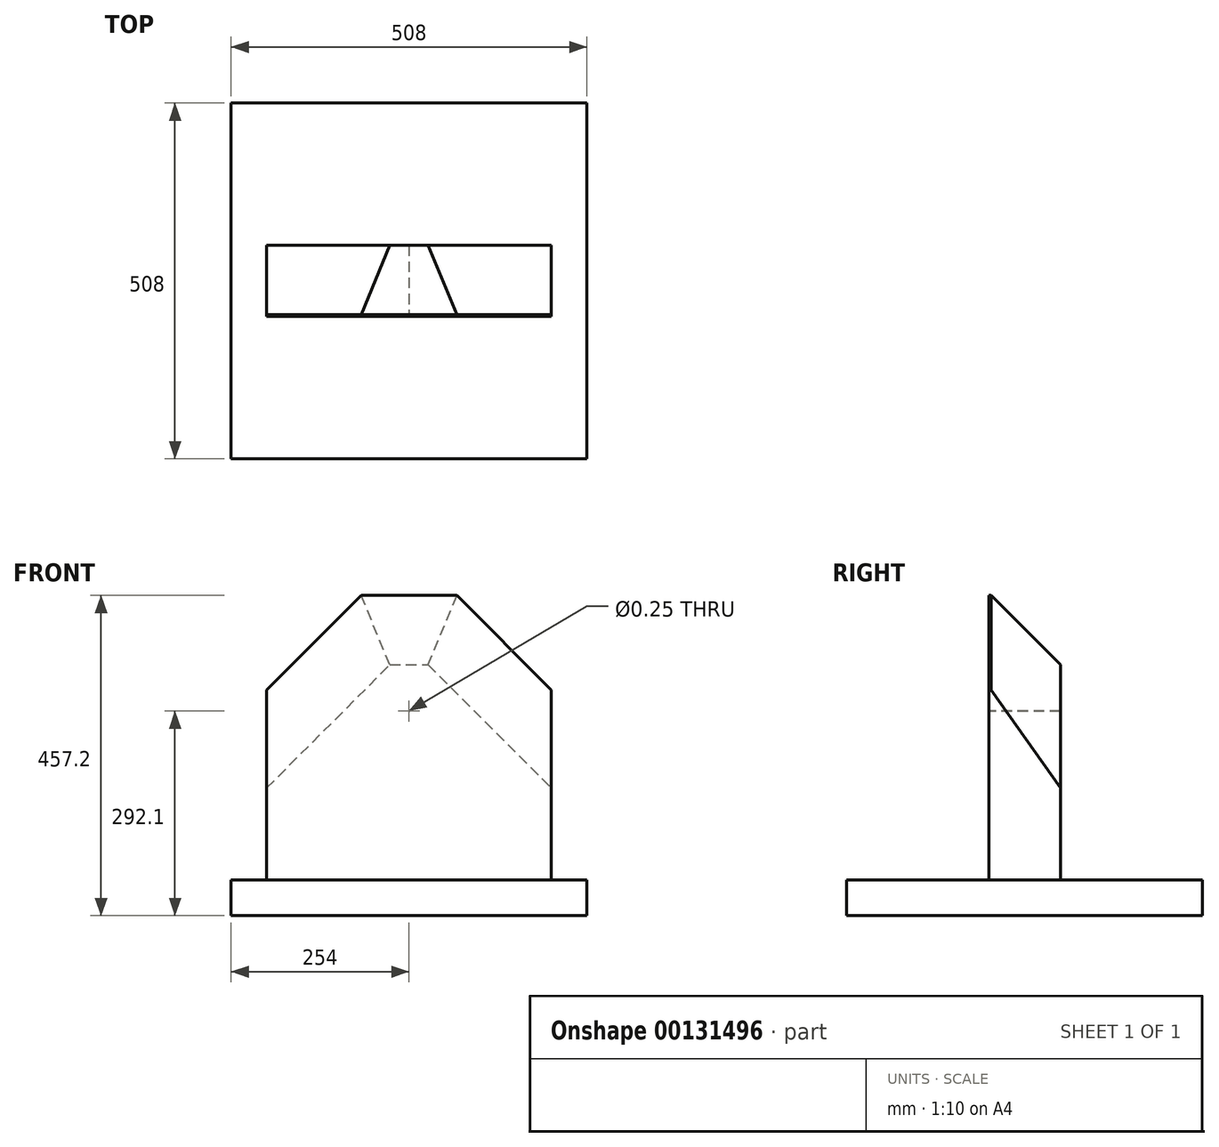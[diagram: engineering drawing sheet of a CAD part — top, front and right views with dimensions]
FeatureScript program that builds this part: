
annotation { "Feature Type Name" : "Feature", "Feature Type Description" : "" }
export const myFeature = defineFeature(function(context is Context, id is Id, definition is map)
    precondition{}
    {
        {
            assignVariable(context, id + "F0", {"name" : "A_Axis", "anyValue" : 60 - 60});
        }
        {
            assignVariable(context, id + "F1", {"name" : "C_Axis", "anyValue" : 35.3 - 35.3});
        }
        {
            var Q0;
            Q0=qCreatedBy(makeId("Top.planeOp"),FACE);
            var sketch = newSketch(context, id + "F2", { "sketchPlane" : qUnion([Q0])});
            skLineSegment(sketch, "E0", {"start": v(0, 0) * mm, "end": v(0, 502.81) * mm, "construction": true});
            skLineSegment(sketch, "E1", {"start": v(0, 0) * mm, "end": v(606.98, 0) * mm, "construction": true});
            skSolve(sketch);
        }
        {
            var Q0;
            Q0=qCreatedBy(makeId("Top.planeOp"),FACE);
            var sketch = newSketch(context, id + "F3", { "sketchPlane" : qUnion([Q0])});
            skLineSegment(sketch, "E2.bottom", {"start": v(254, 254) * mm, "end": v(-254, 254) * mm});
            skLineSegment(sketch, "E2.top", {"start": v(254, -254) * mm, "end": v(-254, -254) * mm});
            skLineSegment(sketch, "E2.left", {"start": v(254, 254) * mm, "end": v(254, -254) * mm});
            skLineSegment(sketch, "E2.right", {"start": v(-254, 254) * mm, "end": v(-254, -254) * mm});
            skPoint(sketch, "E2.middle", {"position": v(0, 0) * mm});
            skSolve(sketch);
        }
        {
            var Q0;
            Q0 = qSketchRegion(id + "F3", true);
            extrude(context, id + "F4", {"entities" : qUnion([Q0]), "depth" : 50.8 * mm});
        }
        {
            var Q0;
            Q0=makeQuery(id+"F4.opExtrude","CAP_FACE",FACE,{"disambiguationData":[OSD([sQuery(id+"F3.wireOp",EDGE,"E2.bottom"),sQuery(id+"F3.wireOp",EDGE,"E2.top"),sQuery(id+"F3.wireOp",EDGE,"E2.left"),sQuery(id+"F3.wireOp",EDGE,"E2.right")])],"isStart":false});
            var sketch = newSketch(context, id + "F5", { "sketchPlane" : qUnion([Q0])});
            skLineSegment(sketch, "E3.bottom", {"start": v(-203.2, 50.8) * mm, "end": v(203.2, 50.8) * mm});
            skLineSegment(sketch, "E3.top", {"start": v(-203.2, -50.8) * mm, "end": v(203.2, -50.8) * mm});
            skLineSegment(sketch, "E3.left", {"start": v(-203.2, 50.8) * mm, "end": v(-203.2, -50.8) * mm});
            skLineSegment(sketch, "E3.right", {"start": v(203.2, 50.8) * mm, "end": v(203.2, -50.8) * mm});
            skPoint(sketch, "E3.middle", {"position": v(0, 0) * mm});
            skSolve(sketch);
        }
        {
            var Q0;
            Q0 = qSketchRegion(id + "F5", true);
            extrude(context, id + "F6", {"entities" : qUnion([Q0]), "operationType" : NewBodyOperationType.ADD, "depth" : 406.4 * mm});
        }
        {
            var Q0;
            Q0=makeQuery(id+"F6.opExtrude","SWEPT_FACE",FACE,{"disambiguationData":[OSD([sQuery(id+"F5.wireOp",EDGE,"E3.top")])]});
            var sketch = newSketch(context, id + "F7", { "sketchPlane" : qUnion([Q0])});
            skLineSegment(sketch, "E4", {"start": v(203.2, 457.2) * mm, "end": v(68.39, 457.2) * mm});
            skLineSegment(sketch, "E5", {"start": v(68.39, 457.2) * mm, "end": v(203.2, 322.39) * mm});
            skLineSegment(sketch, "E6", {"start": v(203.2, 322.39) * mm, "end": v(203.2, 457.2) * mm});
            skLineSegment(sketch, "E7", {"start": v(-203.2, 457.2) * mm, "end": v(-68.39, 457.2) * mm});
            skLineSegment(sketch, "E8", {"start": v(-68.39, 457.2) * mm, "end": v(-203.2, 322.39) * mm});
            skLineSegment(sketch, "E9", {"start": v(-203.2, 322.39) * mm, "end": v(-203.2, 457.2) * mm});
            skPoint(sketch, "E10", {"position": v(0, 292.1) * mm});
            skLineSegment(sketch, "E11", {"start": v(0, 292.1) * mm, "end": v(0, 457.2) * mm, "construction": true});
            skSolve(sketch);
        }
        {
            var Q0;
            Q0 = qSketchRegion(id + "F7", true);
            extrude(context, id + "F8", {"entities" : qUnion([Q0]), "operationType" : NewBodyOperationType.REMOVE, "endBound" : BoundingType.THROUGH_ALL, "oppositeDirection" : true, "depth" : 25.4 * mm});
        }
        {
            var Q0;
            Q0=makeQuery(id+"F6.opExtrude","CAP_EDGE",EDGE,{"disambiguationData":[OSD([sQuery(id+"F5.wireOp",EDGE,"E3.bottom")])],"isStart":false});
            chamfer(context, id + "F9", {"entities" : qUnion([Q0]), "width" : 99.06 * mm, "tangentPropagation" : true});
        }
        {
            var Q0;
            Q0=makeQuery(id+"F8.boolean.opBoolean","INTERSECT",EDGE,{"derivedFrom":[makeQuery(id+"F6.opExtrude","SWEPT_FACE",FACE,{"disambiguationData":[OSD([sQuery(id+"F5.wireOp",EDGE,"E3.bottom")])]}),makeQuery(id+"F8.opExtrude","SWEPT_FACE",FACE,{"disambiguationData":[OSD([sQuery(id+"F7.wireOp",EDGE,"E5")])]})]});
            var Q1;
            Q1=makeQuery(id+"F8.boolean.opBoolean","INTERSECT",EDGE,{"derivedFrom":[makeQuery(id+"F6.opExtrude","SWEPT_FACE",FACE,{"disambiguationData":[OSD([sQuery(id+"F5.wireOp",EDGE,"E3.bottom")])]}),makeQuery(id+"F8.opExtrude","SWEPT_FACE",FACE,{"disambiguationData":[OSD([sQuery(id+"F7.wireOp",EDGE,"E8")])]})]});
            chamfer(context, id + "F10", {"entities" : qUnion([Q0, Q1]), "width" : 99.06 * mm, "tangentPropagation" : true});
        }
        {
            var Q0;
            Q0=makeQuery(id+"F4.opExtrude","SWEPT_BODY",BODY,{"disambiguationData":[OSD([sQuery(id+"F3.wireOp",EDGE,"E2.bottom"),sQuery(id+"F3.wireOp",EDGE,"E2.top"),sQuery(id+"F3.wireOp",EDGE,"E2.left"),sQuery(id+"F3.wireOp",EDGE,"E2.right")])]});
            var Q1;
            Q1=sQuery(id+"F2.wireOp",EDGE,"E1");
            transform(context, id + "F11", {"entities" : qUnion([Q0]), "transformType" : TransformType.ROTATION, "transformAxis" : qUnion([Q1]), "angle" : (getVariable(context, 'A_Axis')) * degree, "makeCopy" : false});
        }
        {
            var Q0;
            Q0=makeQuery(id+"F6.opExtrude","SWEPT_FACE",FACE,{"disambiguationData":[OSD([sQuery(id+"F5.wireOp",EDGE,"E3.bottom")])]});
            cPlane(context, id + "F12", {"entities" : qUnion([Q0]), "cplaneType" : CPlaneType.OFFSET, "offset" : 50.8 * mm, "oppositeDirection" : true, "width" : 152.4 * mm, "height" : 152.4 * mm});
        }
        {
            var Q0;
            Q0=qCreatedBy(id+"F12.planeOp",FACE);
            var sketch = newSketch(context, id + "F13", { "sketchPlane" : qUnion([Q0])});
            skLineSegment(sketch, "E12", {"start": v(0, 0) * mm, "end": v(0, -891.51) * mm});
            skSolve(sketch);
        }
        {
            var Q0;
            Q0=makeQuery(id+"F4.opExtrude","SWEPT_BODY",BODY,{"disambiguationData":[OSD([sQuery(id+"F3.wireOp",EDGE,"E2.bottom"),sQuery(id+"F3.wireOp",EDGE,"E2.top"),sQuery(id+"F3.wireOp",EDGE,"E2.left"),sQuery(id+"F3.wireOp",EDGE,"E2.right")])]});
            var Q1;
            Q1=sQuery(id+"F13.wireOp",EDGE,"E12");
            transform(context, id + "F14", {"entities" : qUnion([Q0]), "transformType" : TransformType.ROTATION, "transformAxis" : qUnion([Q1]), "angle" : (getVariable(context, 'C_Axis')) * degree, "oppositeDirection" : true, "makeCopy" : false});
        }
        {
            var Q0;
            Q0=makeQuery(id+"F6.opExtrude","SWEPT_FACE",FACE,{"disambiguationData":[OSD([sQuery(id+"F5.wireOp",EDGE,"E3.top")])]});
            var sketch = newSketch(context, id + "F15", { "sketchPlane" : qUnion([Q0])});
            skCircle(sketch, "E13", {"center": v(0, 292.1) * mm, "radius": 0.13 * mm});
            skSolve(sketch);
        }
        {
            var Q0;
            Q0 = qSketchRegion(id + "F15", true);
            extrude(context, id + "F16", {"entities" : qUnion([Q0]), "operationType" : NewBodyOperationType.REMOVE, "endBound" : BoundingType.THROUGH_ALL, "oppositeDirection" : true, "depth" : 25.4 * mm});
        }
    });
